# Revit family: Building-ElectricalVehicleCharging-GEWISS-JOINON-ICON_PREMIUM
name_source: partatom
category: Apparecchi elettrici
units: mm (PartAtom-declared; Revit-internal decimal feet)

## family parameters
Condiviso = No
Host = Superficie
Mantenere orientamento annotazione = Sì
Punto di calcolo locali = Sì
Quota connettore circolare = Usa diametro
Taglio con vuoti quando caricato = No
Tipo di parte = Normale

## types (12) — shared parameters
(Auto)restart electrical protections = Currently not present
BLOCCO = B=C
Colour = Dark grey
Customizations: = No
DC Leakage check = Yes
External treatments = No
FORMULA = 1000 mm  [stored 3.28084 ft]
Human Interface = LED RGB + slide touch display
IDF = 800cf01c-04c2-4cf7-a3a7-c80ef5fabb57
INPUT: = -
IP degree = IP55
Immagine tipo = ICON_PREMIUM.jpg
L = 155 mm  [stored 0.50853 ft]
Material = Thermoplastic (Post-industrial origin)
Mechanical characteristics = -
Mouting and installation = Wall mounting (floor mounting with support)
N. of sockets Type 2 = 1
N.poli = 1
OUTPUT : = -
Operating temperature: = -25 +50 °C
POMELLO = bianco
PRESA = Giallo
Produttore = GEWISS S.p.A.
Prospetto di default = 1219 mm
Protection : = DC Leak 6mA
STRUTTURA = RAL - 7035
STRUTTURA ALTA = blue
Shock resistance = IK10
Spostamento_S = 1500 mm  [stored 4.92126 ft]
Thermal-magnetic protection = Currently not present
Type of Socket = Type 2 vandal-proof with shutter
Type of residual current protection = Currently not present
URL = https://www.gewiss.com
VETRO = Vetro
Version file RFA = 19.4
Voltaggio = 0 V
W = 115 mm  [stored 0.377297 ft]

## per-type parameters (varying)
| type | AMBILIGHT | Charging activation | Charging power | Connectivity: | Current supplied (max): | Descrizione | Energy meter | Max power | Modello | Power meter | RFID | Rated current: | Rated insulation voltage (Ui) | Rated voltage | Socket/Connector Nr. (Type) | Terminal blocks: | Total power: |
| GWJ3301A - WB ICON PREM.A. AUT. DLM 4 kW T2S IP55 | Yes | Free access, with dynamic load management | 4,6 kW | BLE | 20 Ampere | WB ICON PREM.A. AUT. DLM 4 kW T2S IP55 |  | 4,6 Chilowatt | GWJ3301A | Currently not present |  | 20 Ampere | 230 Volt | 230 Volt | 1 (Type 2 socket, with shutters) | 3 x 10 mm² | 4,6 Chilowatt |
| GWJ3303A - WB ICON PREM.A. AUT. DLM 11 kW T2S IP55 | Yes | Free access, with dynamic load management | 11 kW | BLE | 16 Ampere | WB ICON PREM.A. AUT. DLM 11 kW T2S IP55 |  | 11 Chilowatt | GWJ3303A | Currently not present |  | 16 Ampere | 400 Volt | 400 Volt | 1 (Type 2 socket, with shutters) | 5 x 10 mm² | 11 Chilowatt |
| GWJ3204W - WB ICON PREM. RFID 22 kW T2S IP55 - 4G |  | Remotely managed, via OCPP 1.6J | 22 kW | LAN,4G | 32 Ampere | WB ICON PREM. RFID 22 kW T2S IP55 - 4G | YES (MID) | 22 Chilowatt | GWJ3204W | YES (MID) | Yes | 32 Ampere | 400 Volt | 400 Volt | 1(Type 2 vandal-proof socket, with shutters) | 5 x 10 mm² | 22 Chilowatt |
| GWJ3202R - WB ICON PREM. RFID 7 kW T2S IP55 |  | Locally managed, via RFID | 7,4 kW | No | 32 Ampere | WB ICON PREM. RFID 7 kW T2S IP55 | YES (MID) | 7,4 Chilowatt | GWJ3202R | YES (MID) | Yes | 32 Ampere | 230 Volt | 230 Volt | 1(Type 2 vandal-proof socket, with shutters) | 3 x 10 mm² | 7,4 Chilowatt |
| GWJ3202L - WB ICON PREM. RFID 7 kW T2S IP55 - ETH |  | Remotely managed, via OCPP 1.6J | 7,4 kW | LAN | 32 Ampere | WB ICON PREM. RFID 7 kW T2S IP55 - ETH | YES (MID) | 7,4 Chilowatt | GWJ3202L | YES (MID) | Yes | 32 Ampere | 230 Volt | 230 Volt | 1(Type 2 vandal-proof socket, with shutters) | 3 x 10 mm² | 7,4 Chilowatt |
| GWJ3202W - WB ICON PREM. RFID 7 kW T2S IP55 - 4G |  | Remotely managed, via OCPP 1.6J | 7,4 kW | LAN,4G | 32 Ampere | WB ICON PREM. RFID 7 kW T2S IP55 - 4G | YES (MID) | 7,4 Chilowatt | GWJ3202W | YES (MID) | Yes | 32 Ampere | 230 Volt | 230 Volt | 1(Type 2 vandal-proof socket, with shutters) | 3 x 10 mm² | 7,4 Chilowatt |
| GWJ3204R - WB ICON PREM. RFID 22 kW T2S IP55 |  | Locally managed, via RFID | 22 kW | No | 32 Ampere | WB ICON PREM. RFID 22 kW T2S IP55 | YES (MID) | 22 Chilowatt | GWJ3204R | YES (MID) | Yes | 32 Ampere | 400 Volt | 400 Volt | 1(Type 2 vandal-proof socket, with shutters) | 5 x 10 mm² | 22 Chilowatt |
| GWJ3201A - WB ICON PREM. AUT. DLM 4 kW T2S IP55 |  | Free access | 4,6 kW | BLE | 20 Ampere | WB ICON PREM. AUT. DLM 4 kW T2S IP55 |  | 4,6 Chilowatt | GWJ3201A | Currently not present |  | 20 Ampere | 230 Volt | 230 Volt | 1 (Type 2 socket, with shutters) | 3 x 10 mm² | 4,6 Chilowatt |
| GWJ3202A - WB ICON PREM. AUT. DLM 7 kW T2S IP55 |  | Free access | 7,4 kW | BLE | 32 Ampere | WB ICON PREM. AUT. DLM 7 kW T2S IP55 |  | 7,4 Chilowatt | GWJ3202A | Currently not present |  | 32 Ampere | 230 Volt | 230 Volt | 1 (Type 2 socket, with shutters) | 3 x 10 mm² | 7,4 Chilowatt |
| GWJ3204L - WB ICON PREM. RFID 22 kW T2S IP55 - ETH |  | Remotely managed, via OCPP 1.6J | 22 kW | LAN | 32 Ampere | WB ICON PREM. RFID 22 kW T2S IP55 - ETH | YES (MID) | 22 Chilowatt | GWJ3204L | YES (MID) | Yes | 32 Ampere | 400 Volt | 400 Volt | 1(Type 2 vandal-proof socket, with shutters) | 5 x 10 mm² | 22 Chilowatt |
| GWJ3203A - WB ICON PREM. AUT. DLM 11 kW T2S IP55 |  | Free access | 11 kW | BLE | 16 Ampere | WB ICON PREM. AUT. DLM 11 kW T2S IP55 |  | 11 Chilowatt | GWJ3203A | Currently not present |  | 16 Ampere | 400 Volt | 400 Volt | 1 (Type 2 socket, with shutters) | 5 x 10 mm² | 11 Chilowatt |
| GWJ3302A - WB ICON PREM.A. AUT. DLM 7 kW T2S IP55 | Yes | Free access, with dynamic load management | 7,4 kW | BLE | 32 Ampere | WB ICON PREM.A. AUT. DLM 7 kW T2S IP55 |  | 7,4 Chilowatt | GWJ3302A | Currently not present |  | 32 Ampere | 230 Volt | 230 Volt | 1 (Type 2 socket, with shutters) | 3 x 10 mm² | 7,4 Chilowatt |

note: [stored X ft] marks values corroborated as IEEE doubles in the binary element streams (Revit-internal decimal feet)

## geometry (parser evidence)
native form markers: Sweep x1
no freeform markers — native parametric forms only
